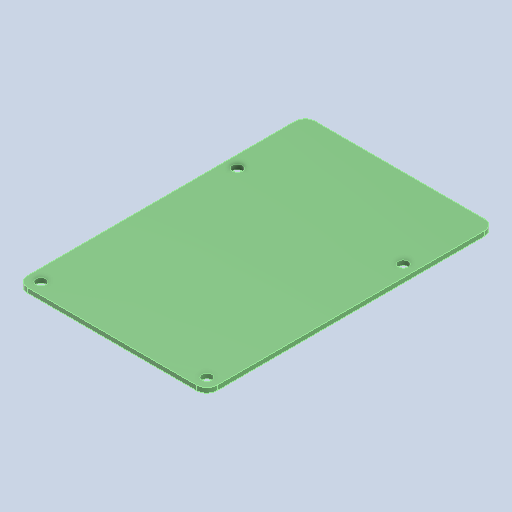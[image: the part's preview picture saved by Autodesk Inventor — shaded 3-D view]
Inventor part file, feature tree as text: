
AUTODESK INVENTOR PART (.ipt)
format: ipt  version: 2022.3 (Build 263350030, 350C)  size: 109,568 bytes
history: native  units: mm
features: sketch x2, extrude x1, fillet x1, hole x1
ambient origin geometry x8: Origin, YZ Plane, XZ Plane, XY Plane, X Axis, Y Axis, Z Axis, Center Point
bodies: Solid1 (feature_tree)
feature tree (5):
  extrude  "Extrusion1"  Depth=56.0mm
  fillet  "Fillet1"  Radius=1.4mm
  hole  "Hole1"  [1 undecoded]
  sketch  "Sketch1"  dims[d0=85.0mm d1=56.0mm d2=1.4mm d3=0.0mm]
  sketch  "Sketch2"  dims[d4=3.0mm d5=49.0mm d6=58.0mm d7=3.5mm d8=3.5mm d9=3.0mm d10=6.0mm d11=4.0mm d12=2.0mm d13=90.0deg d14=6.0mm d15=0.0mm]
note: 1 required parameter value undecoded (feature->parameter linkage not recoverable at this tier; creation-order binding heuristic only, values carry confidence <= 0.55)
